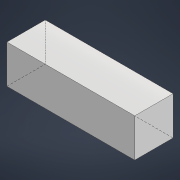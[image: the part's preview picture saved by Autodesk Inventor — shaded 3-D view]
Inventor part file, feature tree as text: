
AUTODESK INVENTOR PART (.ipt)
format: ipt  version: 2022 (Build 260153000, 153)  size: 84,480 bytes
history: native  units: in
note: dims shown in document units (in); Inventor stores cm internally (conversion verified against a paired STEP export)
features: extrude x1, sketch x1
ambient origin geometry x8: Origin, YZ Plane, XZ Plane, XY Plane, X Axis, Y Axis, Z Axis, Center Point
bodies: Solid1 (feature_tree)
feature tree (2):
  extrude  "Extrusion1"  Depth=0.075in
  sketch  "Sketch1"  dims[d0=0.25in d1=0.075in d2=0.075in d3=0.0in]
